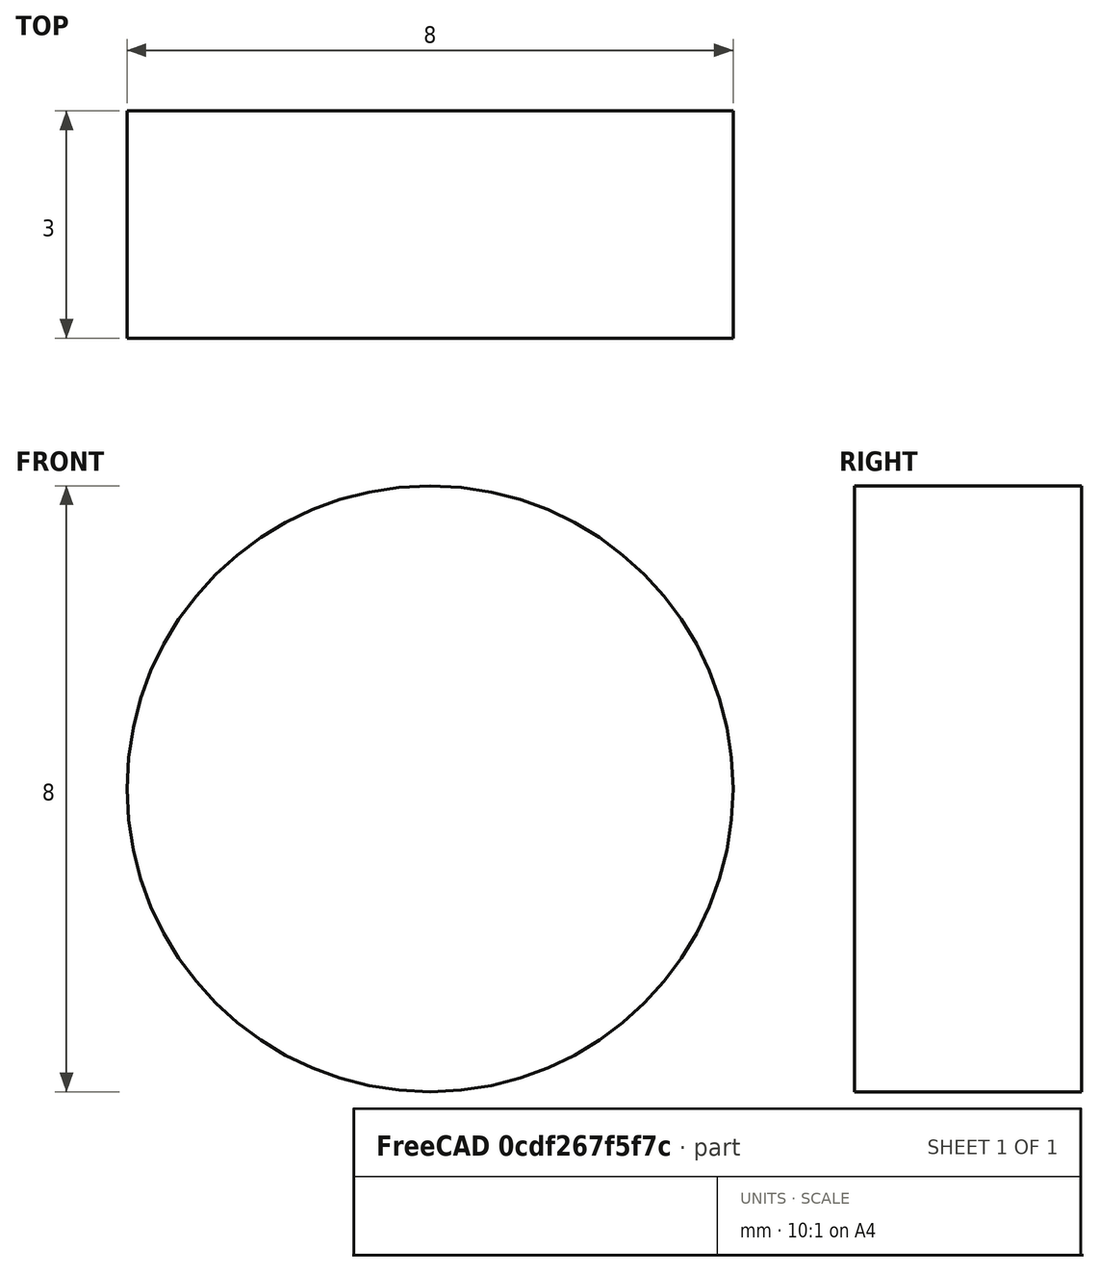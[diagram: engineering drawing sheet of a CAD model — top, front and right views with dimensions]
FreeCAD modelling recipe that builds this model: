
FCSTD DOCUMENT  (FreeCAD 0.18R16093 (Git))
Label: Iman
License: All rights reserved
LicenseURL: http://en.wikipedia.org/wiki/All_rights_reserved
objects: Sketcher::SketchObject×1, PartDesign::Pad×1, PartDesign::Body×1
note: 4 computed .brp shape members not serialized (recipe doc carries the construction recipe); baked Part::Feature solids carry a one-line shape summary decoded from their .brp

FEATURE [Sketcher::SketchObject] Sketch156
  MapMode = 5
  Placement = pos=(0,0,0) rot=(1,0,0;1.5708rad)
  Support = -> [XZ_Plane062]
  sketch-geometry (1):
    g0: Circle CenterX=0 CenterY=0 CenterZ=0 NormalX=0 NormalY=0 NormalZ=1 AngleXU=0 Radius=4
  constraints (2):
    c: Diameter(g0) = 8
    c: Coincident(g0,g-1)
FEATURE [PartDesign::Pad] Pad079
  Length = 3
  Length2 = 100
  Placement = pos=(0,0,0) rot=(1,0,0;1.5708rad)
  Profile = -> Sketch156
  Type = 0
FEATURE [PartDesign::Body] Body063  label="Magnet"
  Group = -> [Sketch156,Pad079]
  Origin = -> Origin063
  Placement = pos=(15,7,22) rot=(0,0,1;0rad)
  Tip = -> Pad079
